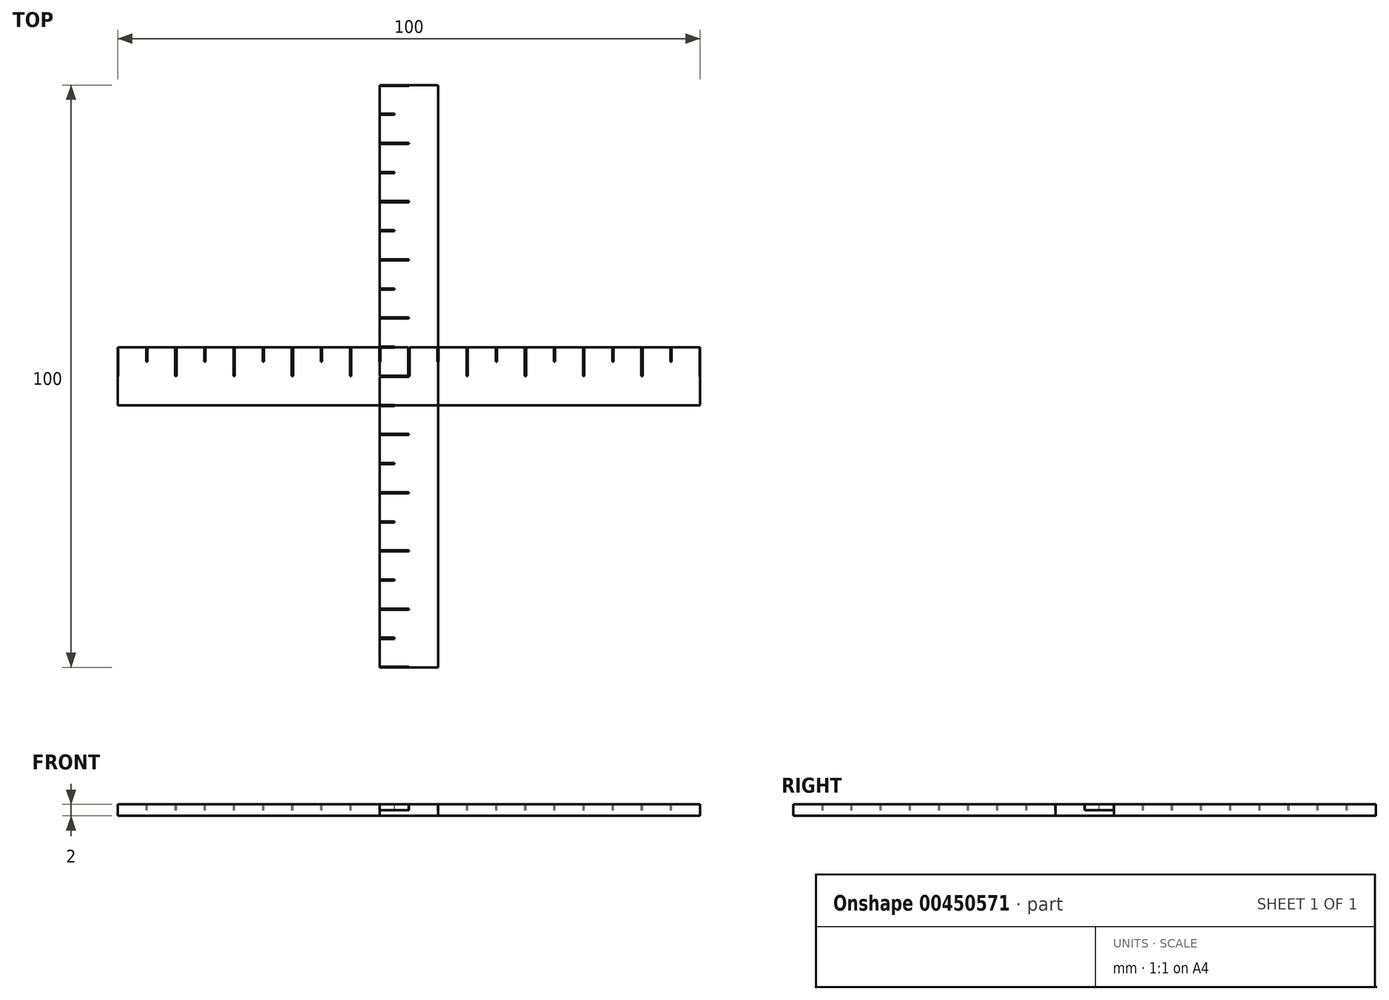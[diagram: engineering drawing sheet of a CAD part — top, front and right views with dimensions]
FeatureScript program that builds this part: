
annotation { "Feature Type Name" : "Feature", "Feature Type Description" : "" }
export const myFeature = defineFeature(function(context is Context, id is Id, definition is map)
    precondition{}
    {
        {
            var Q0;
            Q0=qCreatedBy(makeId("Top.planeOp"),FACE);
            var sketch = newSketch(context, id + "F0", { "sketchPlane" : qUnion([Q0])});
            skLineSegment(sketch, "E0.bottom", {"start": v(50, 5) * mm, "end": v(-50, 5) * mm});
            skLineSegment(sketch, "E0.top", {"start": v(50, -5) * mm, "end": v(-50, -5) * mm});
            skLineSegment(sketch, "E0.left", {"start": v(50, 5) * mm, "end": v(50, -5) * mm});
            skLineSegment(sketch, "E0.right", {"start": v(-50, 5) * mm, "end": v(-50, -5) * mm});
            skPoint(sketch, "E0.middle", {"position": v(0, 0) * mm});
            skSolve(sketch);
        }
        {
            var Q0;
            Q0=makeQuery(id+"F0.imprint","IMPRINT",FACE,{"disambiguationData":[TD([[makeQuery(id+"F0.imprint","IMPRINT",EDGE,{"derivedFrom":sQuery(id+"F0.wireOp",EDGE,"E0.bottom")}),1.0]])]});
            extrude(context, id + "F1", {"entities" : qUnion([Q0]), "depth" : 2 * mm, "offsetDistance" : 25 * mm});
        }
        {
            var Q0;
            Q0=makeQuery(id+"F1.opExtrude","CAP_FACE",FACE,{"disambiguationData":[OSD([sQuery(id+"F0.wireOp",EDGE,"E0.bottom"),sQuery(id+"F0.wireOp",EDGE,"E0.top"),sQuery(id+"F0.wireOp",EDGE,"E0.left"),sQuery(id+"F0.wireOp",EDGE,"E0.right")])],"isStart":false});
            var sketch = newSketch(context, id + "F2", { "sketchPlane" : qUnion([Q0])});
            skLineSegment(sketch, "E1.bottom", {"start": v(-49.9, 5) * mm, "end": v(-50.1, 5) * mm});
            skLineSegment(sketch, "E1.top", {"start": v(-49.9, 0) * mm, "end": v(-50.1, 0) * mm});
            skLineSegment(sketch, "E1.left", {"start": v(-49.9, 5) * mm, "end": v(-49.9, 0) * mm});
            skLineSegment(sketch, "E1.right", {"start": v(-50.1, 5) * mm, "end": v(-50.1, 0) * mm});
            skLineSegment(sketch, "E2.1.0.0", {"start": v(-40.1, 5) * mm, "end": v(-40.1, 0) * mm});
            skLineSegment(sketch, "E2.1.0.1", {"start": v(-39.9, 5) * mm, "end": v(-39.9, 0) * mm});
            skLineSegment(sketch, "E2.1.0.2", {"start": v(-39.9, 0) * mm, "end": v(-40.1, 0) * mm});
            skLineSegment(sketch, "E2.1.0.3", {"start": v(-39.9, 5) * mm, "end": v(-40.1, 5) * mm});
            skLineSegment(sketch, "E2.2.0.0", {"start": v(-30.1, 5) * mm, "end": v(-30.1, 0) * mm});
            skLineSegment(sketch, "E2.2.0.1", {"start": v(-29.9, 5) * mm, "end": v(-29.9, 0) * mm});
            skLineSegment(sketch, "E2.2.0.2", {"start": v(-29.9, 0) * mm, "end": v(-30.1, 0) * mm});
            skLineSegment(sketch, "E2.2.0.3", {"start": v(-29.9, 5) * mm, "end": v(-30.1, 5) * mm});
            skLineSegment(sketch, "E2.3.0.0", {"start": v(-20.1, 5) * mm, "end": v(-20.1, 0) * mm});
            skLineSegment(sketch, "E2.3.0.1", {"start": v(-19.9, 5) * mm, "end": v(-19.9, 0) * mm});
            skLineSegment(sketch, "E2.3.0.2", {"start": v(-19.9, 0) * mm, "end": v(-20.1, 0) * mm});
            skLineSegment(sketch, "E2.3.0.3", {"start": v(-19.9, 5) * mm, "end": v(-20.1, 5) * mm});
            skLineSegment(sketch, "E2.4.0.0", {"start": v(-10.1, 5) * mm, "end": v(-10.1, 0) * mm});
            skLineSegment(sketch, "E2.4.0.1", {"start": v(-9.9, 5) * mm, "end": v(-9.9, 0) * mm});
            skLineSegment(sketch, "E2.4.0.2", {"start": v(-9.9, 0) * mm, "end": v(-10.1, 0) * mm});
            skLineSegment(sketch, "E2.4.0.3", {"start": v(-9.9, 5) * mm, "end": v(-10.1, 5) * mm});
            skLineSegment(sketch, "E2.5.0.0", {"start": v(-0.1, 5) * mm, "end": v(-0.1, 0) * mm});
            skLineSegment(sketch, "E2.5.0.1", {"start": v(0.1, 5) * mm, "end": v(0.1, 0) * mm});
            skLineSegment(sketch, "E2.5.0.2", {"start": v(0.1, 0) * mm, "end": v(-0.1, 0) * mm});
            skLineSegment(sketch, "E2.5.0.3", {"start": v(0.1, 5) * mm, "end": v(-0.1, 5) * mm});
            skLineSegment(sketch, "E2.6.0.0", {"start": v(9.9, 5) * mm, "end": v(9.9, 0) * mm});
            skLineSegment(sketch, "E2.6.0.1", {"start": v(10.1, 5) * mm, "end": v(10.1, 0) * mm});
            skLineSegment(sketch, "E2.6.0.2", {"start": v(10.1, 0) * mm, "end": v(9.9, 0) * mm});
            skLineSegment(sketch, "E2.6.0.3", {"start": v(10.1, 5) * mm, "end": v(9.9, 5) * mm});
            skLineSegment(sketch, "E2.7.0.0", {"start": v(19.9, 5) * mm, "end": v(19.9, 0) * mm});
            skLineSegment(sketch, "E2.7.0.1", {"start": v(20.1, 5) * mm, "end": v(20.1, 0) * mm});
            skLineSegment(sketch, "E2.7.0.2", {"start": v(20.1, 0) * mm, "end": v(19.9, 0) * mm});
            skLineSegment(sketch, "E2.7.0.3", {"start": v(20.1, 5) * mm, "end": v(19.9, 5) * mm});
            skLineSegment(sketch, "E2.8.0.0", {"start": v(29.9, 5) * mm, "end": v(29.9, 0) * mm});
            skLineSegment(sketch, "E2.8.0.1", {"start": v(30.1, 5) * mm, "end": v(30.1, 0) * mm});
            skLineSegment(sketch, "E2.8.0.2", {"start": v(30.1, 0) * mm, "end": v(29.9, 0) * mm});
            skLineSegment(sketch, "E2.8.0.3", {"start": v(30.1, 5) * mm, "end": v(29.9, 5) * mm});
            skLineSegment(sketch, "E2.9.0.0", {"start": v(39.9, 5) * mm, "end": v(39.9, 0) * mm});
            skLineSegment(sketch, "E2.9.0.1", {"start": v(40.1, 5) * mm, "end": v(40.1, 0) * mm});
            skLineSegment(sketch, "E2.9.0.2", {"start": v(40.1, 0) * mm, "end": v(39.9, 0) * mm});
            skLineSegment(sketch, "E2.9.0.3", {"start": v(40.1, 5) * mm, "end": v(39.9, 5) * mm});
            skLineSegment(sketch, "E2.10.0.0", {"start": v(49.9, 5) * mm, "end": v(49.9, 0) * mm});
            skLineSegment(sketch, "E2.10.0.1", {"start": v(50.1, 5) * mm, "end": v(50.1, 0) * mm});
            skLineSegment(sketch, "E2.10.0.2", {"start": v(50.1, 0) * mm, "end": v(49.9, 0) * mm});
            skLineSegment(sketch, "E2.10.0.3", {"start": v(50.1, 5) * mm, "end": v(49.9, 5) * mm});
            skLineSegment(sketch, "E2.direction1", {"start": v(-50.1, 0) * mm, "end": v(-40.1, 0) * mm, "construction": true});
            skLineSegment(sketch, "E3.bottom", {"start": v(-45.1, 5) * mm, "end": v(-44.9, 5) * mm});
            skLineSegment(sketch, "E3.top", {"start": v(-45.1, 2.5) * mm, "end": v(-44.9, 2.5) * mm});
            skLineSegment(sketch, "E3.left", {"start": v(-44.9, 5) * mm, "end": v(-44.9, 2.5) * mm});
            skLineSegment(sketch, "E3.right", {"start": v(-45.1, 5) * mm, "end": v(-45.1, 2.5) * mm});
            skLineSegment(sketch, "E4.1.0.0", {"start": v(-34.9, 5) * mm, "end": v(-34.9, 2.5) * mm});
            skLineSegment(sketch, "E4.1.0.1", {"start": v(-35.1, 5) * mm, "end": v(-35.1, 2.5) * mm});
            skLineSegment(sketch, "E4.1.0.2", {"start": v(-35.1, 2.5) * mm, "end": v(-34.9, 2.5) * mm});
            skLineSegment(sketch, "E4.1.0.3", {"start": v(-35.1, 5) * mm, "end": v(-34.9, 5) * mm});
            skLineSegment(sketch, "E4.2.0.0", {"start": v(-24.9, 5) * mm, "end": v(-24.9, 2.5) * mm});
            skLineSegment(sketch, "E4.2.0.1", {"start": v(-25.1, 5) * mm, "end": v(-25.1, 2.5) * mm});
            skLineSegment(sketch, "E4.2.0.2", {"start": v(-25.1, 2.5) * mm, "end": v(-24.9, 2.5) * mm});
            skLineSegment(sketch, "E4.2.0.3", {"start": v(-25.1, 5) * mm, "end": v(-24.9, 5) * mm});
            skLineSegment(sketch, "E4.3.0.0", {"start": v(-14.9, 5) * mm, "end": v(-14.9, 2.5) * mm});
            skLineSegment(sketch, "E4.3.0.1", {"start": v(-15.1, 5) * mm, "end": v(-15.1, 2.5) * mm});
            skLineSegment(sketch, "E4.3.0.2", {"start": v(-15.1, 2.5) * mm, "end": v(-14.9, 2.5) * mm});
            skLineSegment(sketch, "E4.3.0.3", {"start": v(-15.1, 5) * mm, "end": v(-14.9, 5) * mm});
            skLineSegment(sketch, "E4.4.0.0", {"start": v(-4.9, 5) * mm, "end": v(-4.9, 2.5) * mm});
            skLineSegment(sketch, "E4.4.0.1", {"start": v(-5.1, 5) * mm, "end": v(-5.1, 2.5) * mm});
            skLineSegment(sketch, "E4.4.0.2", {"start": v(-5.1, 2.5) * mm, "end": v(-4.9, 2.5) * mm});
            skLineSegment(sketch, "E4.4.0.3", {"start": v(-5.1, 5) * mm, "end": v(-4.9, 5) * mm});
            skLineSegment(sketch, "E4.5.0.0", {"start": v(5.1, 5) * mm, "end": v(5.1, 2.5) * mm});
            skLineSegment(sketch, "E4.5.0.1", {"start": v(4.9, 5) * mm, "end": v(4.9, 2.5) * mm});
            skLineSegment(sketch, "E4.5.0.2", {"start": v(4.9, 2.5) * mm, "end": v(5.1, 2.5) * mm});
            skLineSegment(sketch, "E4.5.0.3", {"start": v(4.9, 5) * mm, "end": v(5.1, 5) * mm});
            skLineSegment(sketch, "E4.6.0.0", {"start": v(15.1, 5) * mm, "end": v(15.1, 2.5) * mm});
            skLineSegment(sketch, "E4.6.0.1", {"start": v(14.9, 5) * mm, "end": v(14.9, 2.5) * mm});
            skLineSegment(sketch, "E4.6.0.2", {"start": v(14.9, 2.5) * mm, "end": v(15.1, 2.5) * mm});
            skLineSegment(sketch, "E4.6.0.3", {"start": v(14.9, 5) * mm, "end": v(15.1, 5) * mm});
            skLineSegment(sketch, "E4.7.0.0", {"start": v(25.1, 5) * mm, "end": v(25.1, 2.5) * mm});
            skLineSegment(sketch, "E4.7.0.1", {"start": v(24.9, 5) * mm, "end": v(24.9, 2.5) * mm});
            skLineSegment(sketch, "E4.7.0.2", {"start": v(24.9, 2.5) * mm, "end": v(25.1, 2.5) * mm});
            skLineSegment(sketch, "E4.7.0.3", {"start": v(24.9, 5) * mm, "end": v(25.1, 5) * mm});
            skLineSegment(sketch, "E4.8.0.0", {"start": v(35.1, 5) * mm, "end": v(35.1, 2.5) * mm});
            skLineSegment(sketch, "E4.8.0.1", {"start": v(34.9, 5) * mm, "end": v(34.9, 2.5) * mm});
            skLineSegment(sketch, "E4.8.0.2", {"start": v(34.9, 2.5) * mm, "end": v(35.1, 2.5) * mm});
            skLineSegment(sketch, "E4.8.0.3", {"start": v(34.9, 5) * mm, "end": v(35.1, 5) * mm});
            skLineSegment(sketch, "E4.9.0.0", {"start": v(45.1, 5) * mm, "end": v(45.1, 2.5) * mm});
            skLineSegment(sketch, "E4.9.0.1", {"start": v(44.9, 5) * mm, "end": v(44.9, 2.5) * mm});
            skLineSegment(sketch, "E4.9.0.2", {"start": v(44.9, 2.5) * mm, "end": v(45.1, 2.5) * mm});
            skLineSegment(sketch, "E4.9.0.3", {"start": v(44.9, 5) * mm, "end": v(45.1, 5) * mm});
            skLineSegment(sketch, "E4.direction1", {"start": v(-45.1, 2.5) * mm, "end": v(-35.1, 2.5) * mm, "construction": true});
            skSolve(sketch);
        }
        {
            var Q0;
            Q0 = qSketchRegion(id + "F2", true);
            extrude(context, id + "F3", {"entities" : qUnion([Q0]), "operationType" : NewBodyOperationType.REMOVE, "oppositeDirection" : true, "depth" : 1 * mm});
        }
        {
            var Q0;
            Q0=qCreatedBy(makeId("Right.planeOp"),FACE);
            var sketch = newSketch(context, id + "F4", { "sketchPlane" : qUnion([Q0])});
            skLineSegment(sketch, "E5", {"start": v(26.06, 0) * mm, "end": v(-19.6, 0) * mm});
            skLineSegment(sketch, "E6", {"start": v(0, -11.55) * mm, "end": v(0, 11.14) * mm});
            skSolve(sketch);
        }
        {
            var Q0;
            Q0=makeQuery(id+"F1.opExtrude","SWEPT_BODY",BODY,{"disambiguationData":[OSD([sQuery(id+"F0.wireOp",EDGE,"E0.bottom"),sQuery(id+"F0.wireOp",EDGE,"E0.top"),sQuery(id+"F0.wireOp",EDGE,"E0.left"),sQuery(id+"F0.wireOp",EDGE,"E0.right")])]});
            var Q1;
            Q1=qCreatedBy(makeId("Origin.pointOp"),VERTEX);
            var Q2;
            Q2=sQuery(id+"F4.wireOp",EDGE,"E6");
            transform(context, id + "F5", {"entities" : qUnion([Q0]), "transformType" : TransformType.ROTATION, "transformAxis" : qUnion([Q2]), "angle" : 90 * degree, "makeCopy" : true});
        }
    });
